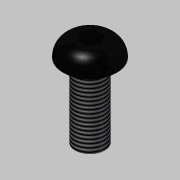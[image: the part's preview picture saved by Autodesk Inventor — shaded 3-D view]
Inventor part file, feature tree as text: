
AUTODESK INVENTOR PART (.ipt)
format: ipt  version: 2014 (Build 180170000, 170)  size: 117,248 bytes
history: native  units: mm
features: extrude x3, sketch x3, fillet x1, thread x1, reference x1
ambient origin geometry x8: Origin, YZ Plane, XZ Plane, XY Plane, X Axis, Y Axis, Z Axis, Center Point
bodies: Solid1 (feature_tree)
feature tree (9):
  extrude  "Extrusion1"  Depth=10.0mm TaperAngle=0.0deg
  extrude  "Extrusion2"  Depth=2.3mm TaperAngle=0.0deg
  fillet  "Fillet1"  Radius=2.2mm
  extrude  "Extrusion4"  Depth=10.0mm TaperAngle=0.0deg
  thread  "Thread1"  [1 undecoded]
  sketch  "Sketch1"  dims[d0=4.0mm d1=10.0mm d2=0.0mm]
  reference  "Reference1"
  sketch  "Sketch2"  dims[d3=7.3mm d4=2.3mm d5=0.0mm d6=2.2mm]
  sketch  "Sketch4"  dims[d10=2.5mm d11=4.0mm d12=0.0mm d13=10.0mm d14=0.0mm]
note: 1 required parameter value undecoded (feature->parameter linkage not recoverable at this tier; creation-order binding heuristic only, values carry confidence <= 0.55)
